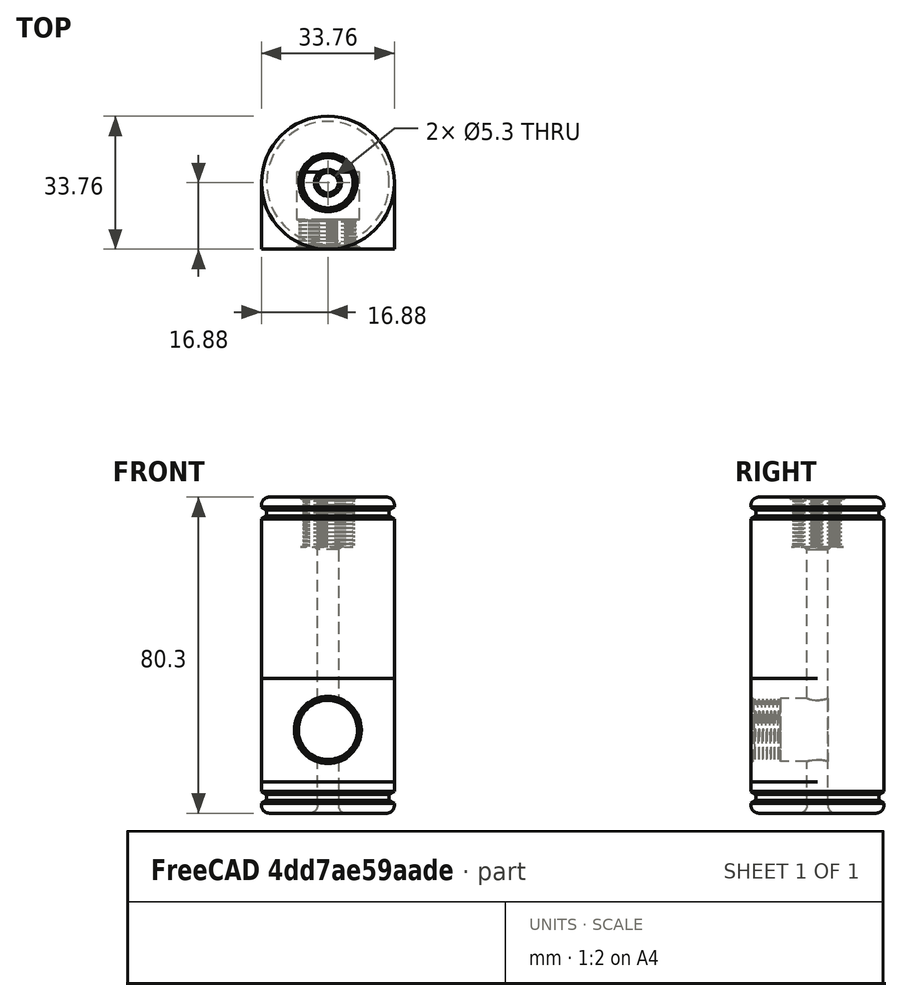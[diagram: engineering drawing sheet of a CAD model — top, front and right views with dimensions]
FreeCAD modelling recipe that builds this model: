
FCSTD DOCUMENT  (FreeCAD 1.0R39285 (Git))
Label: X-O2Sensor_Adapter_Insert_TooBig
License: All rights reserved
LicenseURL: https://en.wikipedia.org/wiki/All_rights_reserved
objects: Sketcher::SketchObject×8, PartDesign::Pocket×4, PartDesign::Pad×3, PartDesign::Chamfer×3, Part::Part2DObjectPython×2, Part::Helix×2, PartDesign::SubtractivePipe×2, PartDesign::Groove×1, Spreadsheet::Sheet×1, PartDesign::Fillet×1, PartDesign::Body×1, App::Part×1
note: 63 computed B-rep shape members (.brp) not serialized (recipe doc carries the construction recipe, not evaluated geometry)

FEATURE [Sketcher::SketchObject] Sketch010
  ArcFitTolerance = 1e-06
  AttacherType = Attacher::AttachEnginePlane
  AttachmentSupport = -> [XY_Plane003]
  FullyConstrained = true
  MakeInternals = false
  MapMode = 5
  expr: Constraints[1] = <<S>>.nipple_thread_diameter + <<S>>.dimension_wall_thickness * 2
  sketch-geometry (1):
    g0: Circle CenterX=0 CenterY=0 CenterZ=0 NormalX=0 NormalY=0 NormalZ=1 AngleXU=0 Radius=16.875
  constraints (2):
    c: Coincident(g0,g-1)
    c: Diameter(g0) = 33.75
FEATURE [PartDesign::Pad] Pad002  label="BasePad"
  AllowMultiFace = true
  AlongSketchNormal = true
  Direction = (0,0,1)
  Length = 8
  Length2 = 10
  Midplane = false
  Offset = 0
  Profile = -> Sketch010
  ReferenceAxis = -> Sketch010 [N_Axis]
  Refine = true
  Reversed = false
  Suppressed = false
  TaperAngle = 0
  TaperAngle2 = 0
  Type = 0
  UseCustomVector = false
  expr: Length = <<S>>.dimension_base_height
FEATURE [Sketcher::SketchObject] Sketch011
  ArcFitTolerance = 1e-06
  AttacherType = Attacher::AttachEnginePlane
  AttachmentSupport = -> [Pad002]
  FullyConstrained = true
  MakeInternals = false
  MapMode = 5
  Placement = pos=(0,0,8) rot=(0,0,1;0rad)
  expr: Constraints[10] = (<<S>>.nipple_thread_diameter + 20) / 2
  expr: Constraints[8] = <<S>>.nipple_thread_diameter + 20
  expr: Constraints[9] = (<<S>>.nipple_thread_diameter + 20) / 2
  sketch-geometry (4):
    g0: LineSegment StartX=-16.875 StartY=2.1e-15 StartZ=0 EndX=-16.875 EndY=-16.875 EndZ=0
    g1: LineSegment StartX=-16.875 StartY=-16.875 StartZ=0 EndX=16.875 EndY=-16.875 EndZ=0
    g2: LineSegment StartX=16.875 StartY=-16.875 StartZ=0 EndX=16.875 EndY=0 EndZ=0
    g3: ArcOfCircle CenterX=0 CenterY=0 CenterZ=0 NormalX=0 NormalY=0 NormalZ=1 AngleXU=0 Radius=16.875 StartAngle=0 EndAngle=3.14159
  constraints (12):
    c: Coincident(g0,g1)
    c: Coincident(g1,g2)
    c: Vertical(g0)
    c: Vertical(g2)
    c: Horizontal(g1)
    c: Coincident(g3,g-1)
    c: Coincident(g3,g2)
    c: Coincident(g3,g0)
    c: DistanceX(g1,g1) = 33.75
    c: DistanceY(g0,g0) = 16.875
    c: DistanceY(g2,g2) = 16.875
    c: DistanceY(g2,g3) = 0
FEATURE [PartDesign::Pad] Pad003  label="SensorSquarePad"
  AllowMultiFace = true
  AlongSketchNormal = true
  BaseFeature = -> Pad002
  Direction = (0,0,1)
  Length = 26.3
  Length2 = 10
  Midplane = false
  Offset = 0
  Profile = -> Sketch011
  ReferenceAxis = -> Sketch011 [N_Axis]
  Refine = true
  Reversed = false
  Suppressed = false
  TaperAngle = 0
  TaperAngle2 = 0
  Type = 0
  UseCustomVector = false
  expr: Length = <<S>>.sensor_smaller_body_diameter
FEATURE [Sketcher::SketchObject] Sketch012
  ArcFitTolerance = 1e-06
  AttacherType = Attacher::AttachEnginePlane
  AttachmentSupport = -> [Pad003]
  FullyConstrained = true
  MakeInternals = false
  MapMode = 5
  Placement = pos=(0,0,34.3) rot=(0,0,1;0rad)
  expr: Constraints[1] = <<S>>.nipple_thread_diameter + 20
  sketch-geometry (1):
    g0: Circle CenterX=0 CenterY=0 CenterZ=0 NormalX=0 NormalY=0 NormalZ=1 AngleXU=0 Radius=16.875
  constraints (2):
    c: Coincident(g0,g-1)
    c: Diameter(g0) = 33.75
FEATURE [PartDesign::Pad] Pad004  label="ExtensionPad"
  AllowMultiFace = true
  AlongSketchNormal = true
  BaseFeature = -> Pad003
  Direction = (0,0,1)
  Length = 46
  Length2 = 10
  Midplane = false
  Offset = 0
  Profile = -> Sketch012
  ReferenceAxis = -> Sketch012 [N_Axis]
  Refine = true
  Reversed = false
  Suppressed = false
  TaperAngle = 0
  TaperAngle2 = 0
  Type = 0
  UseCustomVector = false
  expr: Length = <<S>>.dimension_extender_height
FEATURE [Sketcher::SketchObject] Sketch013
  ArcFitTolerance = 1e-06
  AttacherType = Attacher::AttachEnginePlane
  AttachmentSupport = -> [XZ_Plane003]
  FullyConstrained = true
  MakeInternals = false
  MapMode = 5
  Placement = pos=(0,0,0) rot=(1,0,0;1.5708rad)
  expr: Constraints[37] = (<<S>>.nipple_thread_diameter + <<S>>.dimension_wall_thickness * 2) / 2
  expr: Constraints[40] = <<S>>.dimension_base_height / 2
  expr: Constraints[41] = <<S>>.dimension_base_height + <<S>>.sensor_smaller_body_diameter + <<S>>.dimension_extender_height - <<S>>.dimension_base_height / 2
  sketch-geometry (14):
    g0: LineSegment StartX=18.174 StartY=75.55 StartZ=0 EndX=18.174 EndY=77.05 EndZ=0
    g1: LineSegment StartX=18.174 StartY=77.05 StartZ=0 EndX=16.875 EndY=77.8 EndZ=0
    g2: LineSegment StartX=16.875 StartY=77.8 StartZ=0 EndX=15.576 EndY=77.05 EndZ=0
    g3: LineSegment StartX=15.576 StartY=77.05 StartZ=0 EndX=15.576 EndY=75.55 EndZ=0
    g4: LineSegment StartX=15.576 StartY=75.55 StartZ=0 EndX=16.875 EndY=74.8 EndZ=0
    g5: LineSegment StartX=16.875 StartY=74.8 StartZ=0 EndX=18.174 EndY=75.55 EndZ=0
    g6: Circle [constr] CenterX=16.875 CenterY=76.3 CenterZ=0 NormalX=0 NormalY=0 NormalZ=1 AngleXU=0 Radius=1.5
    g7: LineSegment StartX=18.174 StartY=3.25 StartZ=0 EndX=18.174 EndY=4.75 EndZ=0
    g8: LineSegment StartX=18.174 StartY=4.75 StartZ=0 EndX=16.875 EndY=5.5 EndZ=0
    g9: LineSegment StartX=16.875 StartY=5.5 StartZ=0 EndX=15.576 EndY=4.75 EndZ=0
    g10: LineSegment StartX=15.576 StartY=4.75 StartZ=0 EndX=15.576 EndY=3.25 EndZ=0
    g11: LineSegment StartX=15.576 StartY=3.25 StartZ=0 EndX=16.875 EndY=2.5 EndZ=0
    g12: LineSegment StartX=16.875 StartY=2.5 StartZ=0 EndX=18.174 EndY=3.25 EndZ=0
    g13: Circle [constr] CenterX=16.875 CenterY=4 CenterZ=0 NormalX=0 NormalY=0 NormalZ=1 AngleXU=0 Radius=1.5
  constraints (34):
    c: Coincident(g0,g1)
    c: Coincident(g1,g2)
    c: Coincident(g2,g3)
    c: Coincident(g3,g4)
    c: Coincident(g4,g5)
    c: Coincident(g5,g0)
    c: Equal(g0, g1-g5) x5
    c: PointOnObject(g0,g6)
    c: PointOnObject(g1,g6)
    c: PointOnObject(g2,g6)
    c: PointOnObject(g3,g6)
    c: PointOnObject(g4,g6)
    c: PointOnObject(g5,g6)
    c: Radius(g6) = 1.5
    c: Coincident(g7,g8)
    c: Coincident(g8,g9)
    c: Coincident(g9,g10)
    c: Coincident(g10,g11)
    c: Coincident(g11,g12)
    c: Coincident(g12,g7)
    c: Equal(g7, g8-g12) x5
    c: PointOnObject(g7,g13)
    c: PointOnObject(g8,g13)
    c: PointOnObject(g9,g13)
    c: PointOnObject(g10,g13)
    c: PointOnObject(g11,g13)
    c: PointOnObject(g12,g13)
    c: Radius(g13) = 1.5
    c: DistanceX(g6,g13) = 0
    c: DistanceX(g-1,g13) = 16.875
    c: DistanceX(g7,g7) = 0
    c: DistanceX(g0,g0) = 0
    c: DistanceY(g-1,g13) = 4
    c: DistanceY(g-1,g6) = 76.3
FEATURE [PartDesign::Groove] Groove  label="CaseGrooves"
  AllowMultiFace = true
  Angle = 360
  Angle2 = 60
  Axis = (0,2e-16,1)
  Base = (0,0,0)
  BaseFeature = -> Pad004
  Midplane = false
  Profile = -> Sketch013
  ReferenceAxis = -> Sketch013 [V_Axis]
  Refine = true
  Reversed = false
  Suppressed = false
  Type = 0
FEATURE [Sketcher::SketchObject] Sketch014
  ArcFitTolerance = 1e-06
  AttacherType = Attacher::AttachEnginePlane
  AttachmentSupport = -> [Groove]
  FullyConstrained = true
  MakeInternals = false
  MapMode = 5
  Placement = pos=(0,0,80.3) rot=(0,0,1;0rad)
  expr: Constraints[1] = <<S>>.insert_diameter
  sketch-geometry (1):
    g0: Circle CenterX=0 CenterY=0 CenterZ=0 NormalX=0 NormalY=0 NormalZ=1 AngleXU=0 Radius=2.65
  constraints (2):
    c: Coincident(g0,g-1)
    c: Diameter(g0) = 5.3
FEATURE [PartDesign::Pocket] Pocket008  label="InsertThroughAll"
  AllowMultiFace = true
  AlongSketchNormal = true
  BaseFeature = -> Groove
  Direction = (0,0,-1)
  Length = 5
  Length2 = 5
  Midplane = false
  Offset = 0
  Profile = -> Sketch014
  ReferenceAxis = -> Sketch014 [N_Axis]
  Refine = true
  Reversed = false
  Suppressed = false
  TaperAngle = 0
  TaperAngle2 = 0
  Type = 1
  UseCustomVector = false
FEATURE [Spreadsheet::Sheet] Spreadsheet  label="S"
  cells = A2='zero_width; B2(zero_width)=18; A3='zero_length; B3(zero_length)=23.5; A4='zero_usb_width; B4(zero_usb_width)=9; A5='zero_usb_nib; B5(zero_usb_nib)=1; A6='zero_pcb_thickness; B6(zero_pcb_thickness)=1.15; A7='zero_usb_thickness; B7(zero_usb_thickness)=3.25; C7='This is also the thickest top part; A8='zero_bottom_height; B8(zero_bottom_height)=1.25; A9='zero_bottom_chip_width; B9(zero_bottom_chip_width)=7; A10='zero_pad_width; B10(zero_pad_width)=2.5; A16='ads1115_width; B16(ads1115_width)=28; A17='ads1115_length; B17(ads1115_length)=17.2; A18='ads115_pcb_thickness; B18(ads115_pcb_thickness)=1.5; A19='ads115_holes; B19(ads115_holes)=2.4; A22='charger_width; B22(charger_width)=17.02; A23='charger_length; B23(charger_length)=28; A24='charger_usb_width; B24(charger_usb_width)=9; A25='charger_holes; B25(charger_holes)=1.5; A26='charger_pcb_thickness; B26(charger_pcb_thickness)=1.6; A31='oled_width; B31(oled_width)=27.5; C31='https://thepihut.com/products/blue-0-96-oled-display-module-128x94?srsltid=AfmBOoqjCmrL4VVzqR_EE5hcJSdx-CRojF6zMIyrO1bcx0NnoYyN6zFz; A32='oled_length; B32(oled_length)=27.5; A33='oled_holes; B33(oled_holes)=2; A34='oled_pcb_thickness; B34(oled_pcb_thickness)=1.25; A35='oled_screen_height; B35(oled_screen_height)=1.75; A36='oled_screen_width; B36(oled_screen_width)=24.7; A37='oled_screen_length; B37(oled_screen_length)=16.6; A38='oled_hole_top_edge; B38(oled_hole_top_edge)=1.1; A39='oled_hole_side_edge; B39(oled_hole_side_edge)=1.15; A40='oled_hole_bottom_edge; B40(oled_hole_bottom_edge)=1; A43='battery_width; B43(battery_width)=30; A44='battery_length; B44(battery_length)=42; A45='batter_depth; B45(batter_depth)=8.2; A49='switch_width; B49(switch_width)=11.67; A50='switch_length; B50(switch_length)=18.65; A51='switch_depth; B51(switch_depth)=11.1; A52='swith_length; B52(swith_length)=6; A53='switch_button_diameter; B53(switch_button_diameter)=3.5; A54='switch_button_height; B54(switch_button_height)=1.75; A55='switch_top_thingies; B55(switch_top_thingies)=0.6; A61='vr_back_depth; B61(vr_back_depth)=1.3; A62='vr_hole; B62(vr_hole)=3.7; A63='vr_hole_top_edge; B63(vr_hole_top_edge)=1; A66='sensor_diameter; B66(sensor_diameter)=29.5; A67='sensor_length; B67(sensor_length)=41.5; A68='sensor_thread_diameter; B68(sensor_thread_diameter)=16; A69='sensor_thread_pitch; B69(sensor_thread_pitch)=1; A70='sensor_thread_per_inch; B70(sensor_thread_per_inch)=25.4; A71='sensor_thread_length; B71(sensor_thread_length)=7.5; A72='sensor_smaller_body_diameter; B72(sensor_smaller_body_diameter)=26.3; A75='nipple_pitch; B75(nipple_pitch)=1.41; A76='nipple_thread_diameter; B76(nipple_thread_diameter)=13.75; A77='nipple_thread_per_inch; B77(nipple_thread_per_inch)=18; A78='nipple_thread_length; B78(nipple_thread_length)=12.6; A80='dimension_base_height; B80(dimension_base_height)=8; A81='dimension_extender_height; B81(dimension_extender_height)=46; A83='insert_diameter; B83(insert_diameter)=5.3; A85='dimension_wall_thickness; B85(dimension_wall_thickness)=10
FEATURE [Sketcher::SketchObject] Sketch
  ArcFitTolerance = 1e-06
  AttacherType = Attacher::AttachEnginePlane
  AttachmentSupport = -> [Pocket008]
  FullyConstrained = true
  MakeInternals = false
  MapMode = 5
  Placement = pos=(0,0,80.3) rot=(0,0,1;0rad)
  expr: Constraints[1] = <<S>>.nipple_thread_diameter
  sketch-geometry (1):
    g0: Circle CenterX=0 CenterY=0 CenterZ=0 NormalX=0 NormalY=0 NormalZ=1 AngleXU=0 Radius=6.875
  constraints (2):
    c: Coincident(g0,g-1)
    c: Diameter(g0) = 13.75
FEATURE [PartDesign::Pocket] Pocket  label="NippleThreadChamferPocket"
  AllowMultiFace = true
  AlongSketchNormal = true
  BaseFeature = -> Pocket008
  Direction = (0,0,-1)
  Length = 0.5
  Length2 = 5
  Midplane = false
  Offset = 0
  Profile = -> Sketch
  ReferenceAxis = -> Sketch [N_Axis]
  Refine = true
  Reversed = false
  Suppressed = false
  TaperAngle = 0
  TaperAngle2 = 0
  Type = 0
  UseCustomVector = false
FEATURE [PartDesign::Chamfer] Chamfer  label="NippleThreadChamfer"
  Angle = 45
  Base = -> Pocket [Edge37]
  BaseFeature = -> Pocket
  ChamferType = 0
  FlipDirection = false
  Refine = true
  Size = 0.4999
  Size2 = 1
  SupportTransform = false
  Suppressed = false
  UseAllEdges = false
FEATURE [Part::Part2DObjectPython] VThreadProfile  # WARN: FeaturePython — macro-defined, semantics opaque (R4)
  Area = 138.565
  AttacherType = Attacher::AttachEnginePlane
  AttachmentSupport = -> [Chamfer]
  Closed = true
  Continuity = C2
  Deviation = 0.1
  Height = 12.6
  Helix = Helix
  InternalOrExternal = 0
  MajorDiameter = 13.75
  MajorDiameterFinal = 13.95
  MakeFace = true
  MapMode = 11
  MinorDiameter = 12.5954
  MinorDiameterFinal = 12.7954
  Parameterization = 1
  Pitch = 1
  Placement = pos=(9e-16,0,80.3) rot=(0.707107,-0.707107,0;3.14159rad)
  Presets = 0
  Quality = 11
  ThreadCount = 12.6
  Tolerance = 0.2
  Variants = 0
  Version = 1.96
  d_delta = 1.15459
  expr: Height = <<S>>.nipple_thread_length
  expr: MajorDiameter = <<S>>.nipple_thread_diameter
FEATURE [Part::Helix] Helix
  Angle = 0
  AttacherType = Attacher::AttachEngine3D
  AttachmentSupport = -> [Chamfer]
  Height = 12.6
  Length = 80.1645
  LocalCoord = 0
  MapMode = 11
  Pitch = 1
  Placement = pos=(9e-16,0,80.3) rot=(0.707107,-0.707107,0;3.14159rad)
  Radius = 1
  SegmentLength = 1
  Style = 0
  expr: AttachmentOffset = VThreadProfile.AttachmentOffset
  expr: AttachmentSupport = VThreadProfile.AttachmentSupport
  expr: Height = VThreadProfile.ThreadCount * VThreadProfile.Pitch
  expr: MapMode = VThreadProfile.MapMode
  expr: MapPathParameter = VThreadProfile.MapPathParameter
  expr: MapReversed = VThreadProfile.MapReversed
  expr: Pitch = VThreadProfile.Pitch
  expr: SegmentLength = 1
FEATURE [PartDesign::SubtractivePipe] SubtractivePipe  label="NippleThreads"
  AllowMultiFace = true
  AuxilleryCurvelinear = true
  AuxillerySpineTangent = false
  BaseFeature = -> Chamfer
  Binormal = (0,0,0)
  Midplane = false
  Mode = 2
  Profile = -> VThreadProfile
  Refine = true
  Reversed = false
  Spine = -> Helix [Edge1,Edge2,Edge3,Edge4,Edge5,Edge6,Edge7,Edge8,Edge9,Edge10,Edge11,Edge12,Edge13]
  SpineTangent = false
  Suppressed = false
  Transformation = 0
  Transition = 0
FEATURE [PartDesign::Chamfer] Chamfer001  label="InsertLeadInChamfer"
  Angle = 45
  Base = -> SubtractivePipe [Edge69]
  BaseFeature = -> SubtractivePipe
  ChamferType = 0
  FlipDirection = false
  Refine = true
  Size = 0.75
  Size2 = 1
  SupportTransform = false
  Suppressed = false
  UseAllEdges = false
FEATURE [Sketcher::SketchObject] Sketch015
  ArcFitTolerance = 1e-06
  AttacherType = Attacher::AttachEnginePlane
  AttachmentSupport = -> [Chamfer001]
  FullyConstrained = true
  MakeInternals = false
  MapMode = 5
  Placement = pos=(0,-16.875,0) rot=(1,0,0;1.5708rad)
  expr: Constraints[1] = <<S>>.dimension_base_height + <<S>>.sensor_smaller_body_diameter / 2
  expr: Constraints[2] = <<S>>.sensor_thread_diameter
  sketch-geometry (1):
    g0: Circle CenterX=0 CenterY=21.15 CenterZ=0 NormalX=0 NormalY=0 NormalZ=1 AngleXU=0 Radius=8
  constraints (3):
    c: PointOnObject(g0,g-2)
    c: DistanceY(g-1,g0) = 21.15
    c: Diameter(g0) = 16
FEATURE [PartDesign::Pocket] Pocket009  label="SensorThreadChamferPocket"
  AllowMultiFace = true
  AlongSketchNormal = true
  BaseFeature = -> Chamfer001
  Direction = (0,1,-2e-16)
  Length = 0.5
  Length2 = 5
  Midplane = false
  Offset = 0
  Profile = -> Sketch015
  ReferenceAxis = -> Sketch015 [N_Axis]
  Refine = true
  Reversed = false
  Suppressed = false
  TaperAngle = 0
  TaperAngle2 = 0
  Type = 0
  UseCustomVector = false
FEATURE [PartDesign::Chamfer] Chamfer002  label="SensorThreadChamfer"
  Angle = 45
  Base = -> Pocket009 [Edge49]
  BaseFeature = -> Pocket009
  ChamferType = 0
  FlipDirection = false
  Refine = true
  Size = 0.4999
  Size2 = 1
  SupportTransform = false
  Suppressed = false
  UseAllEdges = false
FEATURE [Part::Part2DObjectPython] VThreadProfile001  # WARN: FeaturePython — macro-defined, semantics opaque (R4)
  Area = 189.457
  AttacherType = Attacher::AttachEnginePlane
  AttachmentSupport = -> [Chamfer002]
  Closed = true
  Continuity = C2
  Deviation = 0.1
  Height = 7.5
  Helix = Helix001
  InternalOrExternal = 0
  MajorDiameter = 16
  MajorDiameterFinal = 16.2
  MakeFace = true
  MapMode = 11
  MinorDiameter = 14.8454
  MinorDiameterFinal = 15.0454
  Parameterization = 1
  Pitch = 1
  Placement = pos=(0,-16.875,21.15) rot=(0.57735,-0.57735,-0.57735;4.18879rad)
  Presets = 0
  Quality = 11
  ThreadCount = 7.5
  Tolerance = 0.2
  Variants = 0
  Version = 1.96
  d_delta = 1.15459
  expr: Height = <<S>>.sensor_thread_length
  expr: MajorDiameter = <<S>>.sensor_thread_diameter
FEATURE [Part::Helix] Helix001
  Angle = 0
  AttacherType = Attacher::AttachEngine3D
  AttachmentSupport = -> [Chamfer002]
  Height = 7.5
  Length = 47.717
  LocalCoord = 0
  MapMode = 11
  Pitch = 1
  Placement = pos=(0,-16.875,21.15) rot=(0.57735,-0.57735,-0.57735;4.18879rad)
  Radius = 1
  SegmentLength = 1
  Style = 0
  expr: AttachmentOffset = VThreadProfile001.AttachmentOffset
  expr: AttachmentSupport = VThreadProfile001.AttachmentSupport
  expr: Height = VThreadProfile001.ThreadCount * VThreadProfile001.Pitch
  expr: MapMode = VThreadProfile001.MapMode
  expr: MapPathParameter = VThreadProfile001.MapPathParameter
  expr: MapReversed = VThreadProfile001.MapReversed
  expr: Pitch = VThreadProfile001.Pitch
  expr: SegmentLength = 1
FEATURE [PartDesign::SubtractivePipe] SubtractivePipe001
  AllowMultiFace = true
  AuxilleryCurvelinear = true
  AuxillerySpineTangent = false
  BaseFeature = -> Chamfer002
  Binormal = (0,0,0)
  Midplane = false
  Mode = 2
  Profile = -> VThreadProfile001
  Refine = true
  Reversed = false
  Spine = -> Helix001 [Edge1,Edge2,Edge3,Edge4,Edge5,Edge6,Edge7,Edge8]
  SpineTangent = false
  Suppressed = false
  Transformation = 0
  Transition = 0
FEATURE [Sketcher::SketchObject] Sketch016
  ArcFitTolerance = 1e-06
  AttacherType = Attacher::AttachEnginePlane
  AttachmentSupport = -> [SubtractivePipe001]
  FullyConstrained = true
  MakeInternals = false
  MapMode = 5
  Placement = pos=(-1.71056e-10,-9.375,4.17534e-09) rot=(1,0,0;1.5708rad)
  expr: Constraints[1] = <<S>>.dimension_base_height + <<S>>.sensor_smaller_body_diameter / 2
  expr: Constraints[2] = <<S>>.sensor_thread_diameter
  sketch-geometry (1):
    g0: Circle CenterX=0 CenterY=21.15 CenterZ=0 NormalX=0 NormalY=0 NormalZ=1 AngleXU=0 Radius=8
  constraints (3):
    c: PointOnObject(g0,g-2)
    c: DistanceY(g-1,g0) = 21.15
    c: Diameter(g0) = 16
FEATURE [PartDesign::Pocket] Pocket010  label="SensorAirPocket"
  AllowMultiFace = true
  AlongSketchNormal = true
  BaseFeature = -> SubtractivePipe001
  Direction = (1.8246e-11,1,-4.45369e-10)
  Length = 12.025
  Length2 = 5
  Midplane = false
  Offset = 0
  Profile = -> Sketch016
  ReferenceAxis = -> Sketch016 [N_Axis]
  Refine = true
  Reversed = false
  Suppressed = false
  TaperAngle = 0
  TaperAngle2 = 0
  Type = 0
  UseCustomVector = false
  expr: Length = -<<S>>.sensor_thread_length + (<<S>>.nipple_thread_diameter + <<S>>.dimension_wall_thickness * 2) / 2 + <<S>>.insert_diameter / 2
FEATURE [PartDesign::Fillet] Fillet  label="EndFillets"
  Base = -> Pocket010 [Edge57,Edge55,Edge61]
  BaseFeature = -> Pocket010
  Radius = 2
  Refine = true
  SupportTransform = false
  Suppressed = false
  UseAllEdges = false
FEATURE [PartDesign::Body] Body001  label="SensorHeadInsertBody"
  AllowCompound = false
  Group = -> [Sketch010,Pad002,Sketch011,Pad003,Sketch012,Pad004,Sketch013,Groove,Sketch014,Pocket008,Sketch,Pocket,Chamfer,VThreadProfile,Helix,SubtractivePipe,Chamfer001,Sketch015,Pocket009,Chamfer002,VThreadProfile001,Helix001,SubtractivePipe001,Sketch016,Pocket010,Fillet]
  Origin = -> Origin003
  Tip = -> Fillet
FEATURE [App::Part] Part001  label="SensorHeadInsert"
  Group = -> [Body001]
  Origin = -> Origin002
